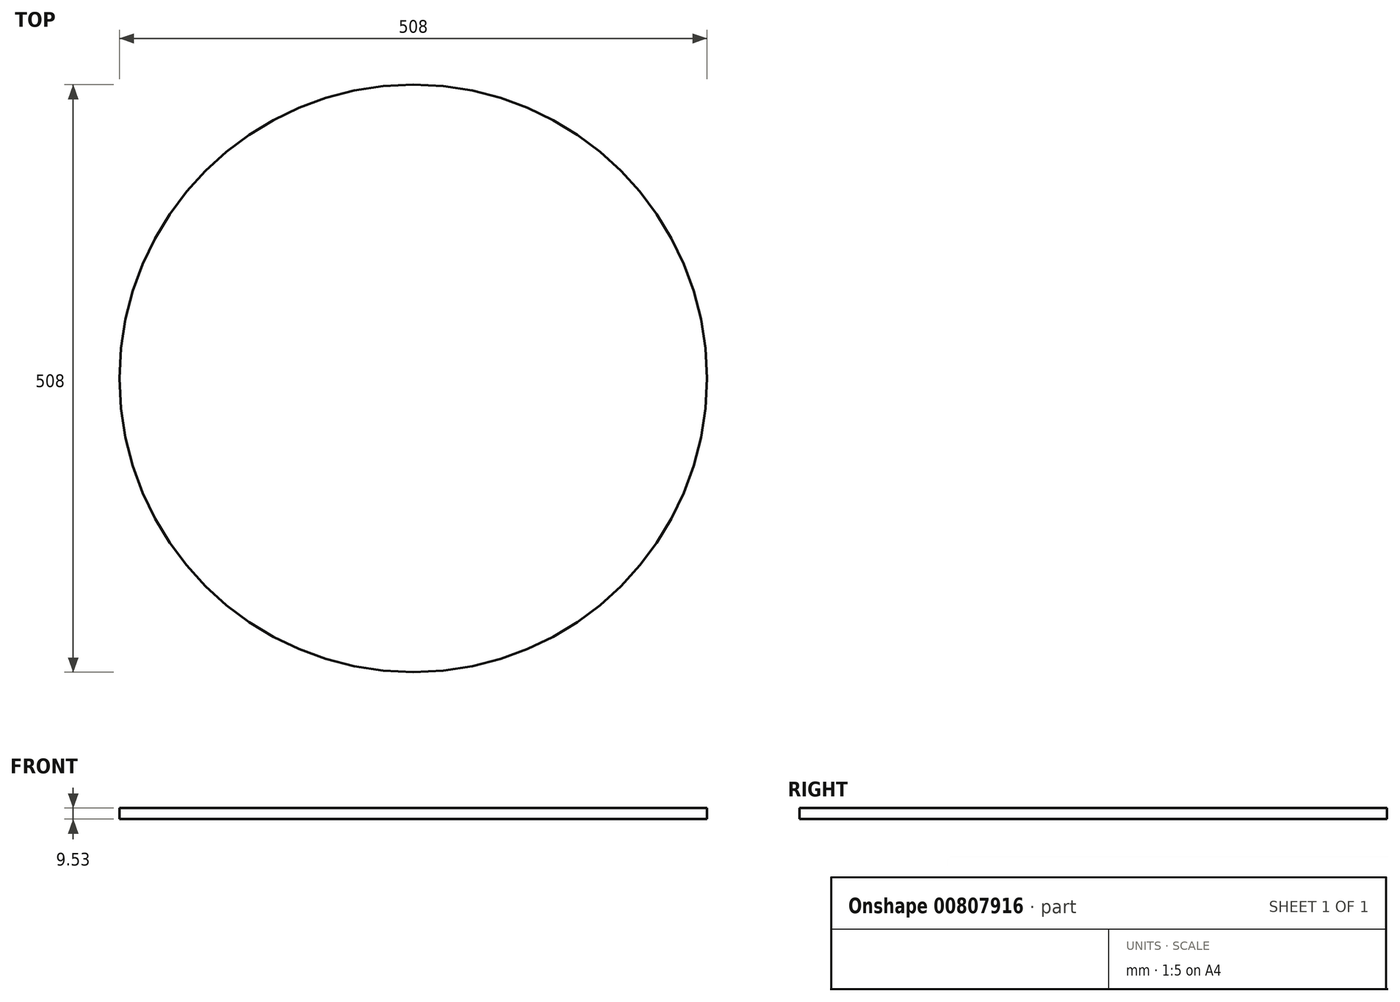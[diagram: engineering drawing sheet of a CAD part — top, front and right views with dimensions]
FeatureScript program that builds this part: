
annotation { "Feature Type Name" : "Feature", "Feature Type Description" : "" }
export const myFeature = defineFeature(function(context is Context, id is Id, definition is map)
    precondition{}
    {
        {
            var Q0;
            Q0=qCreatedBy(makeId("Top.planeOp"),FACE);
            var sketch = newSketch(context, id + "F0", { "sketchPlane" : qUnion([Q0])});
            skCircle(sketch, "E0", {"center": v(0, 0) * mm, "radius": 254 * mm});
            skLineSegment(sketch, "E1", {"start": v(0, 0) * mm, "end": v(118.86, 136.82) * mm});
            skLineSegment(sketch, "E2", {"start": v(0, 0) * mm, "end": v(184.9, 0) * mm});
            skLineSegment(sketch, "E3", {"start": v(0, 0) * mm, "end": v(127.54, -110.8) * mm});
            skLineSegment(sketch, "E4", {"start": v(0, 0) * mm, "end": v(0, -457.2) * mm});
            skSolve(sketch);
        }
        {
            var Q0;
            Q0=makeQuery(id+"F0.imprint","IMPRINT",FACE,{"disambiguationData":[TD([[makeQuery(id+"F0.imprint","IMPRINT",EDGE,{"derivedFrom":sQuery(id+"F0.wireOp",EDGE,"E0")}),1.0]])]});
            extrude(context, id + "F1", {"entities" : qUnion([Q0]), "depth" : 9.52 * mm, "offsetDistance" : 25.4 * mm});
        }
    });
